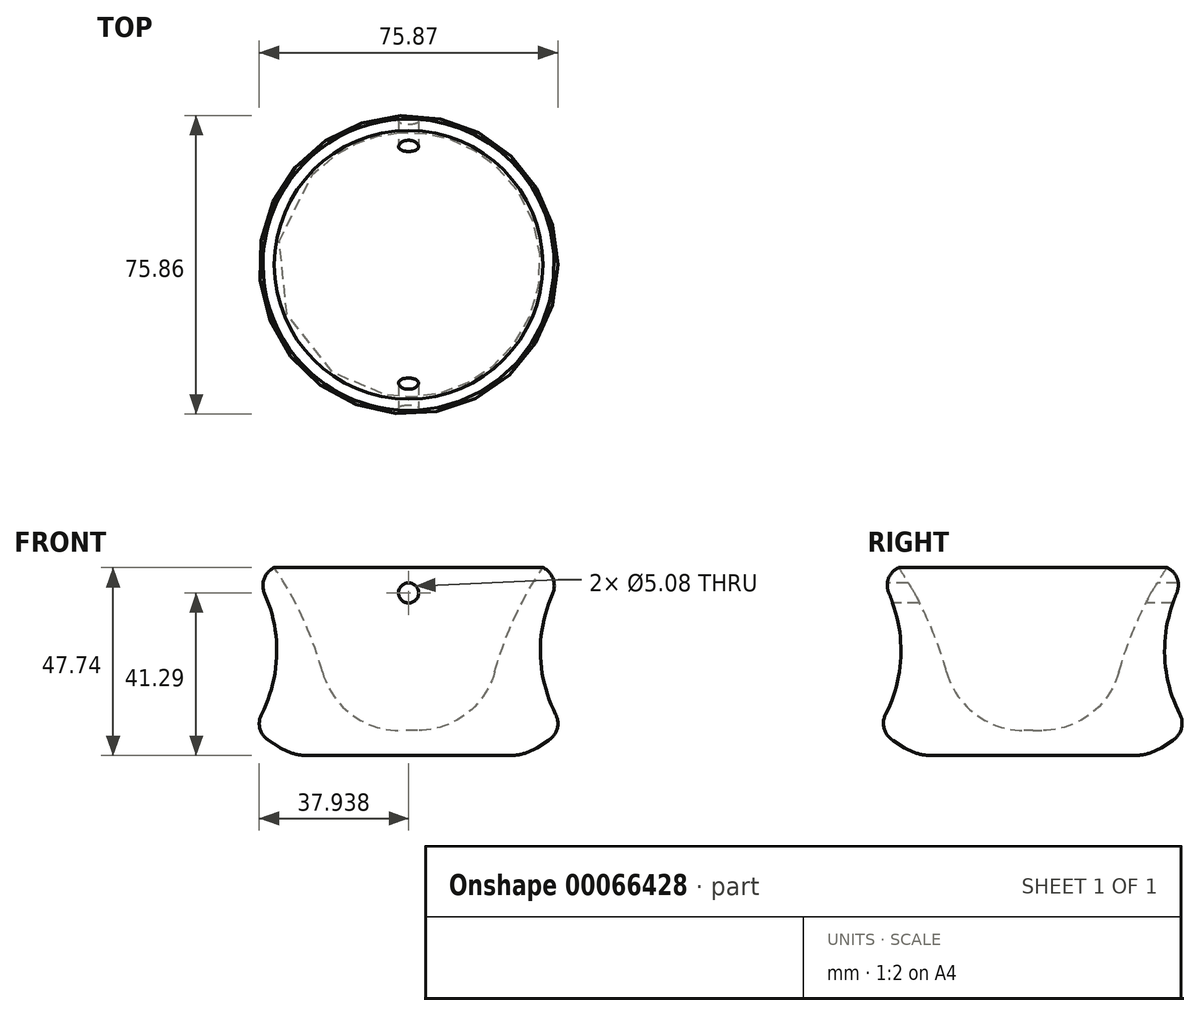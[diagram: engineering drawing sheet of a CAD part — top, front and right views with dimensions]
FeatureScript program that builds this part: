
annotation { "Feature Type Name" : "Feature", "Feature Type Description" : "" }
export const myFeature = defineFeature(function(context is Context, id is Id, definition is map)
    precondition{}
    {
        {
            var Q0;
            Q0=qCreatedBy(makeId("Front.planeOp"),FACE);
            var sketch = newSketch(context, id + "F0", { "sketchPlane" : qUnion([Q0])});
            skLineSegment(sketch, "E0", {"start": v(-5.27, -41.29) * mm, "end": v(13.78, -41.29) * mm});
            skLineSegment(sketch, "E1", {"start": v(-22.65, 6.45) * mm, "end": v(-16.3, 6.45) * mm});
            skLineSegment(sketch, "E2", {"start": v(-1.23, -34.94) * mm, "end": v(17.82, -34.94) * mm});
            skLineSegment(sketch, "E3", {"start": v(13.78, -41.29) * mm, "end": v(17.82, -41.29) * mm});
            skLineSegment(sketch, "E4", {"start": v(17.82, -34.94) * mm, "end": v(17.82, -41.29) * mm});
            skLineSegment(sketch, "E5", {"start": v(17.82, -26.78) * mm, "end": v(17.82, -10.52) * mm});
            skLineSegment(sketch, "E6", {"start": v(-5.27, -41.29) * mm, "end": v(-11.7, -41.29) * mm});
            skArc(sketch, "E7", {"start": v(-1.23, -34.94) * mm, "mid": v(-6.23, -13.33) * mm, "end": v(-16.3, 6.45) * mm});
            skPoint(sketch, "E8.start.orphan", {"position": v(-7.58, -34.94) * mm});
            skLineSegment(sketch, "E9", {"start": v(-11.7, -41.29) * mm, "end": v(-21.92, -34.8) * mm});
            skArc(sketch, "E10", {"start": v(-21.92, -34.8) * mm, "mid": v(-15.67, -14.06) * mm, "end": v(-22.65, 6.45) * mm});
            skSolve(sketch);
        }
        {
            var Q0;
            Q0=qCreatedBy(makeId("Front.planeOp"),FACE);
            var sketch = newSketch(context, id + "F1", { "sketchPlane" : qUnion([Q0])});
            skLineSegment(sketch, "E11", {"start": v(0, 0) * mm, "end": v(17.82, 0) * mm});
            skCircle(sketch, "E12", {"center": v(17.82, 0) * mm, "radius": 2.54 * mm});
            skSolve(sketch);
        }
        {
            var Q0;
            Q0=qSketchRegion(id+"F0",true);
            var Q1;
            Q1=sQuery(id+"F0.wireOp",EDGE,"E5");
            revolve(context, id + "F2", {"entities" : qUnion([Q0]), "axis" : qUnion([Q1]), "revolveType" : RevolveType.FULL});
        }
        {
            var Q0;
            Q0=makeQuery(id+"F1.imprint","IMPRINT",FACE,{"disambiguationData":[TD([[makeQuery(id+"F1.imprint","IMPRINT",EDGE,{"derivedFrom":sQuery(id+"F1.wireOp",EDGE,"E12")}),1.0]])]});
            extrude(context, id + "F3", {"entities" : qUnion([Q0]), "operationType" : NewBodyOperationType.REMOVE, "oppositeDirection" : true, "depth" : 127 * mm, "hasSecondDirection" : true, "secondDirectionOppositeDirection" : false, "secondDirectionDepth" : 127 * mm});
        }
        {
            var Q0;
            Q0=makeQuery(id+"F2.opRevolve","SWEPT_EDGE",EDGE,{"disambiguationData":[OSD([sQuery(id+"F0.wireOp",EDGE,"E2"),sQuery(id+"F0.wireOp",EDGE,"E7")])]});
            fillet(context, id + "F4", {"entities" : qUnion([Q0]), "radius" : 20.32 * mm, "tangentPropagation" : true, "allowEdgeOverflow" : false});
        }
        {
            var Q0;
            Q0=makeQuery(id+"F2.opRevolve","SWEPT_EDGE",EDGE,{"disambiguationData":[OSD([sQuery(id+"F0.wireOp",EDGE,"E1"),sQuery(id+"F0.wireOp",EDGE,"E10")])]});
            fillet(context, id + "F5", {"entities" : qUnion([Q0]), "radius" : 5.08 * mm, "tangentPropagation" : true, "allowEdgeOverflow" : false});
        }
        {
            var Q0;
            Q0=makeQuery(id+"F2.opRevolve","SWEPT_EDGE",EDGE,{"disambiguationData":[OSD([sQuery(id+"F0.wireOp",EDGE,"E9"),sQuery(id+"F0.wireOp",EDGE,"E10")])]});
            fillet(context, id + "F6", {"entities" : qUnion([Q0]), "radius" : 5.08 * mm, "tangentPropagation" : true, "allowEdgeOverflow" : false});
        }
        {
            var Q0;
            Q0=makeQuery(id+"F2.opRevolve","SWEPT_EDGE",EDGE,{"disambiguationData":[OSD([sQuery(id+"F0.wireOp",EDGE,"E6"),sQuery(id+"F0.wireOp",EDGE,"E9")])]});
            fillet(context, id + "F7", {"entities" : qUnion([Q0]), "radius" : 12.7 * mm, "tangentPropagation" : true, "allowEdgeOverflow" : false});
        }
    });
